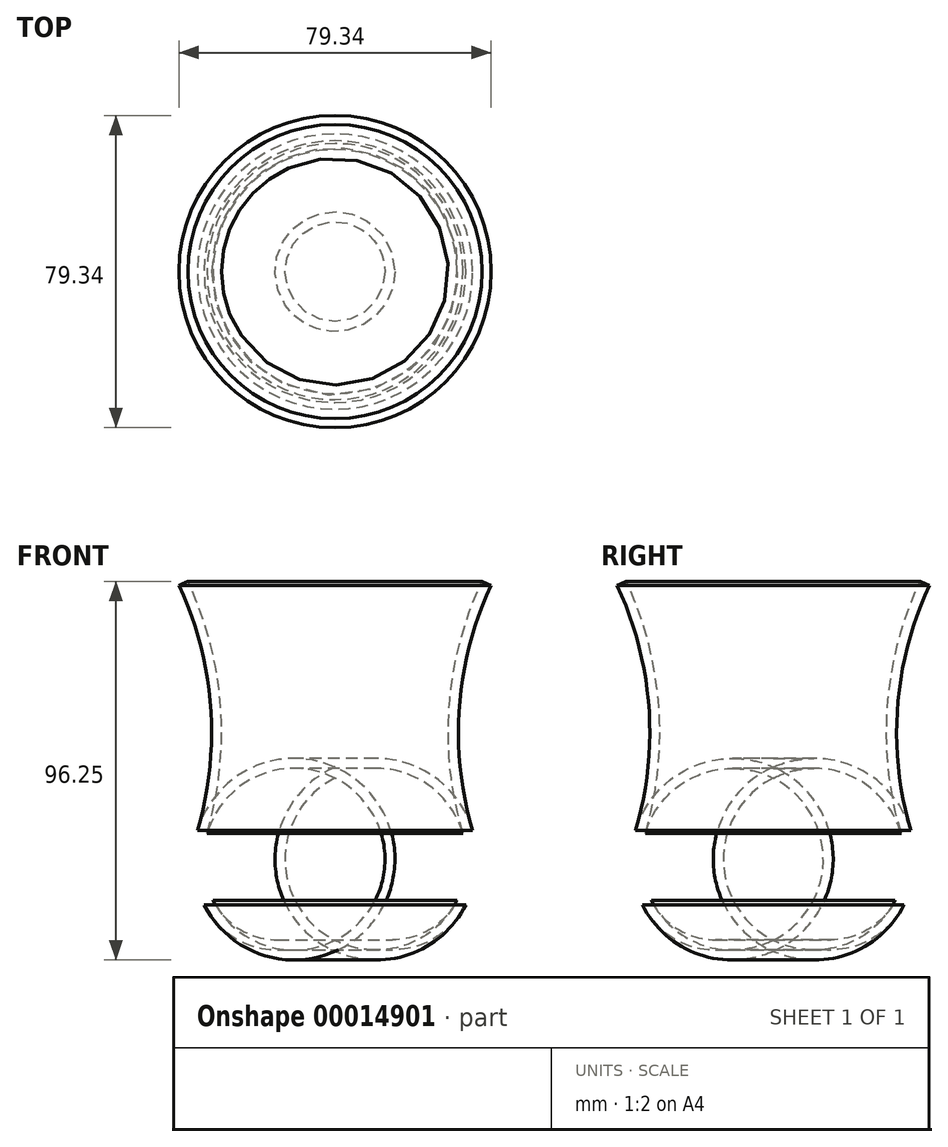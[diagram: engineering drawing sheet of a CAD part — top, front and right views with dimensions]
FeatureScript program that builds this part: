
annotation { "Feature Type Name" : "Feature", "Feature Type Description" : "" }
export const myFeature = defineFeature(function(context is Context, id is Id, definition is map)
    precondition{}
    {
        {
            var Q0;
            Q0=qCreatedBy(makeId("Front.planeOp"),FACE);
            var sketch = newSketch(context, id + "F0", { "sketchPlane" : qUnion([Q0])});
            skLineSegment(sketch, "E0", {"start": v(0, 0) * mm, "end": v(14.62, 0) * mm});
            skArc(sketch, "E1", {"start": v(14.62, 0) * mm, "mid": v(25.55, 3.09) * mm, "end": v(33.25, 11.44) * mm});
            skArc(sketch, "E2", {"start": v(33.25, 11.44) * mm, "mid": v(35.9, 20.7) * mm, "end": v(34.96, 30.28) * mm});
            skArc(sketch, "E3", {"start": v(34.96, 30.28) * mm, "mid": v(31.6, 61.86) * mm, "end": v(39.67, 92.57) * mm});
            skArc(sketch, "E4.0", {"start": v(32.52, 29.56) * mm, "mid": v(29.07, 62.05) * mm, "end": v(37.37, 93.65) * mm});
            skArc(sketch, "E4.1", {"start": v(30.98, 12.6) * mm, "mid": v(33.37, 20.93) * mm, "end": v(32.52, 29.56) * mm});
            skArc(sketch, "E4.2", {"start": v(14.62, 2.54) * mm, "mid": v(24.22, 5.25) * mm, "end": v(30.98, 12.6) * mm});
            skLineSegment(sketch, "E4.3", {"start": v(0, 2.54) * mm, "end": v(14.62, 2.54) * mm});
            skLineSegment(sketch, "E5", {"start": v(0, 0) * mm, "end": v(0, 2.54) * mm});
            skLineSegment(sketch, "E6", {"start": v(39.67, 92.57) * mm, "end": v(37.37, 93.65) * mm});
            skSolve(sketch);
        }
        {
            var Q0;
            Q0=makeQuery(id+"F0.imprint","IMPRINT",FACE,{"disambiguationData":[TD([[makeQuery(id+"F0.imprint","IMPRINT",EDGE,{"derivedFrom":sQuery(id+"F0.wireOp",EDGE,"E0")}),1.0]])]});
            var Q1;
            Q1=sQuery(id+"F0.wireOp",EDGE,"E5");
            revolve(context, id + "F1", {"entities" : qUnion([Q0]), "axis" : qUnion([Q1]), "revolveType" : RevolveType.FULL});
        }
    });
